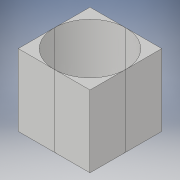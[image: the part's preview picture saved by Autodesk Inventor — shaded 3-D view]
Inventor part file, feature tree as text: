
AUTODESK INVENTOR PART (.ipt)
format: ipt  version: 2017 (Build 210142000, 142)  size: 95,232 bytes
history: native  units: in
note: dims shown in document units (in); Inventor stores cm internally (conversion verified against a paired STEP export)
features: extrude x1, sketch x1
ambient origin geometry x8: Origin, YZ Plane, XZ Plane, XY Plane, X Axis, Y Axis, Z Axis, Center Point
bodies: Solid1 (feature_tree)
feature tree (2):
  extrude  "Extrusion1"  Depth=69.0in
  sketch  "Sketch1"  dims[d0=69.0in d1=69.0in d2=69.0in d3=0.0in]
